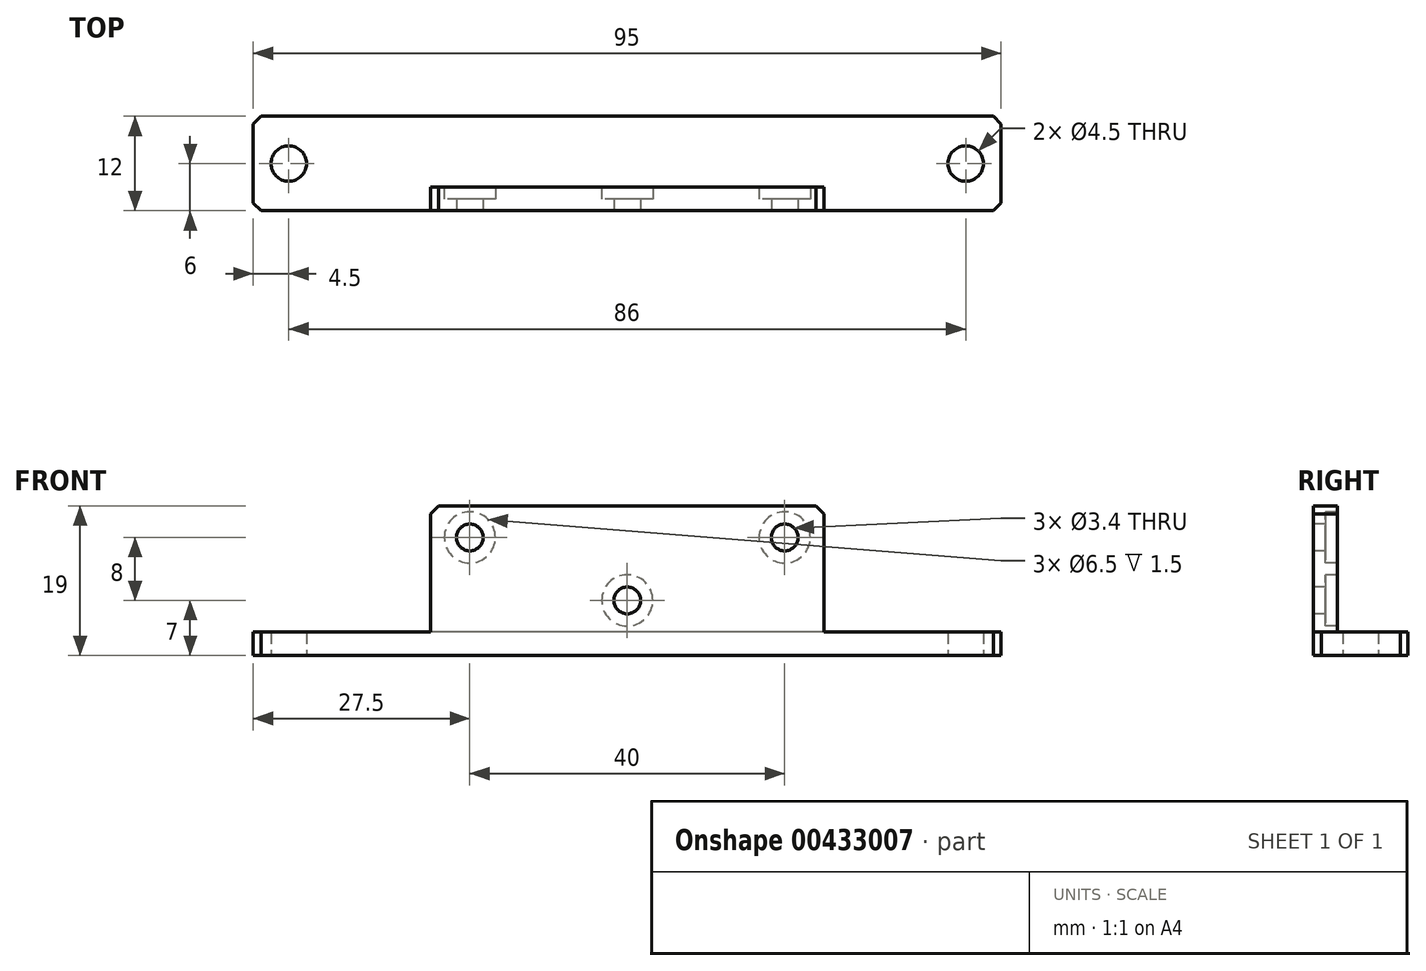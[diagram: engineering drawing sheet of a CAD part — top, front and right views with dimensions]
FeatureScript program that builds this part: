
annotation { "Feature Type Name" : "Feature", "Feature Type Description" : "" }
export const myFeature = defineFeature(function(context is Context, id is Id, definition is map)
    precondition{}
    {
        {
            var Q0;
            Q0=qCreatedBy(makeId("Front.planeOp"),FACE);
            var sketch = newSketch(context, id + "F0", { "sketchPlane" : qUnion([Q0])});
            skLineSegment(sketch, "E0.bottom", {"start": v(47.5, -6) * mm, "end": v(-47.5, -6) * mm});
            skLineSegment(sketch, "E0.top", {"start": v(47.5, 6) * mm, "end": v(-47.5, 6) * mm});
            skLineSegment(sketch, "E0.left", {"start": v(47.5, -6) * mm, "end": v(47.5, 6) * mm});
            skLineSegment(sketch, "E0.right", {"start": v(-47.5, -6) * mm, "end": v(-47.5, 6) * mm});
            skPoint(sketch, "E0.middle", {"position": v(0, 0) * mm});
            skPoint(sketch, "E1", {"position": v(-43, 0) * mm});
            skCircle(sketch, "E2", {"center": v(-43, 0) * mm, "radius": 2.25 * mm});
            skCircle(sketch, "E3.MirrorC", {"center": v(43, 0) * mm, "radius": 2.25 * mm});
            skSolve(sketch);
        }
        {
            var Q0;
            Q0=makeQuery(id+"F0.imprint","IMPRINT",FACE,{"disambiguationData":[TD([[makeQuery(id+"F0.imprint","IMPRINT",EDGE,{"derivedFrom":sQuery(id+"F0.wireOp",EDGE,"E0.bottom")}),-1.0]])]});
            extrude(context, id + "F1", {"entities" : qUnion([Q0]), "oppositeDirection" : true, "depth" : 3 * mm, "offsetDistance" : 25 * mm});
        }
        {
            var Q0;
            Q0=makeQuery(id+"F1.opExtrude","CAP_FACE",FACE,{"disambiguationData":[OSD([sQuery(id+"F0.wireOp",EDGE,"E0.bottom"),sQuery(id+"F0.wireOp",EDGE,"E0.top"),sQuery(id+"F0.wireOp",EDGE,"E0.left"),sQuery(id+"F0.wireOp",EDGE,"E0.right"),sQuery(id+"F0.wireOp",EDGE,"E2"),sQuery(id+"F0.wireOp",EDGE,"E3.MirrorC")])],"isStart":false});
            var sketch = newSketch(context, id + "F2", { "sketchPlane" : qUnion([Q0])});
            skLineSegment(sketch, "E4.bottom", {"start": v(-25, 6) * mm, "end": v(25, 6) * mm});
            skLineSegment(sketch, "E4.top", {"start": v(-25, 3) * mm, "end": v(25, 3) * mm});
            skLineSegment(sketch, "E4.left", {"start": v(-25, 6) * mm, "end": v(-25, 3) * mm});
            skLineSegment(sketch, "E4.right", {"start": v(25, 6) * mm, "end": v(25, 3) * mm});
            skSolve(sketch);
        }
        {
            var Q0;
            Q0=makeQuery(id+"F2.imprint","IMPRINT",FACE,{"disambiguationData":[TD([[makeQuery(id+"F2.imprint","IMPRINT",EDGE,{"derivedFrom":sQuery(id+"F2.wireOp",EDGE,"E4.bottom")}),-1.0]])]});
            extrude(context, id + "F3", {"entities" : qUnion([Q0]), "operationType" : NewBodyOperationType.ADD, "depth" : 16 * mm, "offsetDistance" : 25 * mm});
        }
        {
            var Q0;
            Q0=makeQuery(id+"F1.opExtrude","SWEPT_EDGE",EDGE,{"disambiguationData":[OSD([sQuery(id+"F0.wireOp",EDGE,"E0.bottom"),sQuery(id+"F0.wireOp",EDGE,"E0.left")])]});
            var Q1;
            Q1=makeQuery(id+"F1.opExtrude","SWEPT_EDGE",EDGE,{"disambiguationData":[OSD([sQuery(id+"F0.wireOp",EDGE,"E0.top"),sQuery(id+"F0.wireOp",EDGE,"E0.left")])]});
            var Q2;
            Q2=makeQuery(id+"F3.opExtrude","CAP_EDGE",EDGE,{"disambiguationData":[OSD([sQuery(id+"F2.wireOp",EDGE,"E4.left")])],"isStart":false});
            var Q3;
            Q3=makeQuery(id+"F3.opExtrude","CAP_EDGE",EDGE,{"disambiguationData":[OSD([sQuery(id+"F2.wireOp",EDGE,"E4.right")])],"isStart":false});
            var Q4;
            Q4=makeQuery(id+"F1.opExtrude","SWEPT_EDGE",EDGE,{"disambiguationData":[OSD([sQuery(id+"F0.wireOp",EDGE,"E0.bottom"),sQuery(id+"F0.wireOp",EDGE,"E0.right")])]});
            var Q5;
            Q5=makeQuery(id+"F1.opExtrude","SWEPT_EDGE",EDGE,{"disambiguationData":[OSD([sQuery(id+"F0.wireOp",EDGE,"E0.top"),sQuery(id+"F0.wireOp",EDGE,"E0.right")])]});
            chamfer(context, id + "F4", {"entities" : qUnion([Q0, Q1, Q2, Q3, Q4, Q5]), "width" : 1 * mm, "tangentPropagation" : true});
        }
        {
            var Q0;
            Q0=makeQuery(id+"F3.opExtrude","SWEPT_FACE",FACE,{"disambiguationData":[OSD([sQuery(id+"F2.wireOp",EDGE,"E4.top")])]});
            var sketch = newSketch(context, id + "F5", { "sketchPlane" : qUnion([Q0])});
            skPoint(sketch, "E5", {"position": v(0, -7) * mm});
            skPoint(sketch, "E6", {"position": v(-20, -15) * mm});
            skPoint(sketch, "E7.MirrorP", {"position": v(20, -15) * mm});
            skSolve(sketch);
        }
        {
            var Q0;
            Q0=sQuery(id+"F5.wireOp",VERTEX,"E5");
            var Q1;
            Q1=sQuery(id+"F5.wireOp",VERTEX,"E6");
            var Q2;
            Q2=sQuery(id+"F5.wireOp",VERTEX,"E7.MirrorP");
            var Q3;
            Q3=makeQuery(id+"F1.opExtrude","SWEPT_BODY",BODY,{"disambiguationData":[OSD([sQuery(id+"F0.wireOp",EDGE,"E0.bottom"),sQuery(id+"F0.wireOp",EDGE,"E0.top"),sQuery(id+"F0.wireOp",EDGE,"E0.left"),sQuery(id+"F0.wireOp",EDGE,"E0.right"),sQuery(id+"F0.wireOp",EDGE,"E2"),sQuery(id+"F0.wireOp",EDGE,"E3.MirrorC")])]});
            hole(context, id + "F6", {"style" : HoleStyle.C_BORE, "endStyle" : HoleEndStyle.BLIND, "holeDiameter" : 3.4 * mm, "cBoreDiameter" : 6.5 * mm, "cBoreDepth" : 1.5 * mm, "majorDiameter" : 4 * mm, "holeDepth" : 14.1 * mm, "tappedDepth" : 12 * mm, "tapClearance" : 3, "locations" : qUnion([Q0, Q1, Q2]), "scope" : qUnion([Q3]), "startStyle" : HoleStartStyle.PART});
        }
        {
            var Q0;
            Q0=makeQuery(id+"FY8rNK0ButV288v.importOp","IMPORT",FACE,{"importTag":0.0});
            cPoint(context, id + "F7", {"pointType" : PointType.MESH_POINT, "mesh" : qUnion([Q0]), "x" : -25 * mm, "y" : 8.5 * mm, "z" : 3 * mm});
        }
        {
            var Q0;
            Q0=makeQuery(id+"F1.opExtrude","SWEPT_BODY",BODY,{"disambiguationData":[OSD([sQuery(id+"F0.wireOp",EDGE,"E0.bottom"),sQuery(id+"F0.wireOp",EDGE,"E0.top"),sQuery(id+"F0.wireOp",EDGE,"E0.left"),sQuery(id+"F0.wireOp",EDGE,"E0.right"),sQuery(id+"F0.wireOp",EDGE,"E2"),sQuery(id+"F0.wireOp",EDGE,"E3.MirrorC")])]});
            var Q1;
            {var subQ0=sQuery(id+"F2.wireOp",EDGE,"E4.right");Q1=makeQuery(id+"F4.opChamfer","BLEND_VERTEX",VERTEX,{"blendedFrom":[makeQuery(id+"F3.opExtrude","CAP_EDGE",EDGE,{"disambiguationData":[OSD([subQ0])],"isStart":false}),makeQuery(id+"F3.opExtrude","SWEPT_FACE",FACE,{"disambiguationData":[OSD([sQuery(id+"F2.wireOp",EDGE,"E4.top")])]}),makeQuery(id+"F3.opExtrude","SWEPT_FACE",FACE,{"disambiguationData":[OSD([subQ0])]})],"blendedInto":[makeQuery(id+"F3.opExtrude","SWEPT_FACE",FACE,{"disambiguationData":[OSD([sQuery(id+"F2.wireOp",EDGE,"E4.top")])]}),makeQuery(id+"F3.opExtrude","SWEPT_FACE",FACE,{"disambiguationData":[OSD([subQ0])]})]});}
            var Q2;
            Q2 = qCreatedBy(id + "F7" ,VERTEX);
            var Q3;
            Q3=makeQuery(id+"F1.opExtrude","CAP_EDGE",EDGE,{"disambiguationData":[OSD([sQuery(id+"F0.wireOp",EDGE,"E0.top")])],"isStart":true});
            transform(context, id + "F8", {"entities" : qUnion([Q0]), "transformType" : TransformType.ROTATION, "transformAxis" : qUnion([Q3]), "angle" : 90 * degree, "oppositeDirection" : true, "makeCopy" : false});
        }
    });
